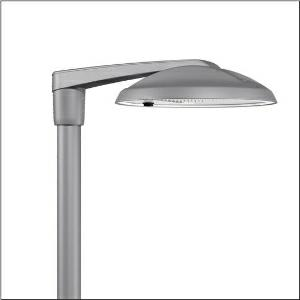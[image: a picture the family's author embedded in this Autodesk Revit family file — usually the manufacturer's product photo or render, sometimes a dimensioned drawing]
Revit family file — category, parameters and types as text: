
# Revit family: dl_r__50_iq_mini___st1_0a_5xa248d31u08ne_2837
name_source: partatom
category: Lighting Fixtures
units: mm (PartAtom-declared; Revit-internal decimal feet)

## family parameters
Cut with Voids When Loaded = No
Host = Face
Light Source = No
Part Type = Normal
Room Calculation Point = No
Round Connector Dimension = Use Diameter
Shared = No

## types (1)
- --- (1 x LED, 17900 lm, 110.1 W, 3000K)
    Apparent Load = 110 VA
    CIE Flux Codes = 37 72 97 100 100
    Color Rendering = 70
    Color Temperature = 3000K
    Default Elevation = 1800 mm
    Description = DL® 50 iQ mini, mast luminaire, primary light control with lens, of PMMA, primary optical cover: cover, of toughened safety glass, transparent, light distribution: ST1.0a, light emission: direct distribution, primary light characteristic: asymmetric, installation type: post-top, side-entry, LED, High Power LED, rated luminous flux: 17.900lm, luminous efficacy: 163lm/W, light colour: 730, colour temperature: 3000K, control gear: iQ-Street Remote, D4i with power reduction, control: optimised constant luminous flux control (CLO 2.0), Desk-Remote (wireless, voltage-free reading and setting of iQ features in the workshop via application-optimized NFC function/RFID function), Light-Fading, Smart-Wire, Night-Set, Lumen-Switch, Temp-Guard, Auto-Match, Street-Remote, pre-setting: logarithmic dimming characteristic, mains connection: 220..240V, AC, 50/60Hz, connection cable pre-assembled, cable length: 10,5m, start of lifetime: 110W, end of service life: 116W, reduction: 50W, luminaire housing, of diecast aluminium, powder-coated, Siteco® metallic grey (DB 702S), inclination adjustable: 0°, 5°, 10° (post-top) | 0°, -5°, -10°, -15° (side-entry), please order mast post-top element or mast side-entry element separately, diameter: 500mm, height: 115mm, post-top: for spigot size d x l = 76 x 100mm; with reducer (optional accessory) 60 x 100mm | side-entry: for spigot size d x l = 60 x 100mm; with reducer (optional accessory) 42 x 100mm, mounting height: 4..6m, Smart Interface below, protection rating (complete): IP66, insulation class (complete): insulation class II (safety insulation), certification: CE, ENEC, ENEC+, VDE, impact resistance: IK08, permissible operating ambient temperature for outdoor applications: -25..+40°C, standard-compliant lighting for roads and squares, packaging unit: 1 piece

Light Distribution: ST1.0a
    Height = 115 mm
    Lamp = 1 x LED
    Lamp Light Flux = 17900 lm
    Lamp Power = 110.1 W
    Lamp count = 1
    Length = 500 mm
    Luminous efficacy = 163 lm/W
    Manufacturer = Siteco
    ModVariant = No
    Model = 5XA248D31U08NE
    Number of Poles = 1
    OnlyDefault = Yes
    Power Factor = 1
    Product Name = DL® 50 iQ mini | ST1.0a
    Product group = mast luminaire | pylon top
    ProductGroupID = 6100
    Protection Class = Protection class II
    Protection Degree = IP 66
    RLX_Detail_Level = 1
    RLX_Emergency_Light_Flux = 0 lm
    RLX_Emergency_Type = 0
    RLX_Emergency_Type_DB = No
    RlxData = <blob elided: 106721 chars, md5=0ca37c4e>
    Socket = socket
    Standby Power = 0 W
    System Light Flux = 17900 lm
    System Power = 110 W
    Type Comments = factory setting: luminous flux: 100 % | dim-lin: 254 | 601 mA
    Type Image = l_1296955.jpg
    URL = http://relux.com
    VarID = @adj_086623
    Voltage = 0 V
    Weight = 0.00 kg
    Width = 0 mm  [stored 0 ft]

note: [stored X ft] marks values corroborated as IEEE doubles in the binary element streams (Revit-internal decimal feet)

## geometry (parser evidence)
native form markers: Blend x4, Sweep x11
no freeform markers — native parametric forms only
